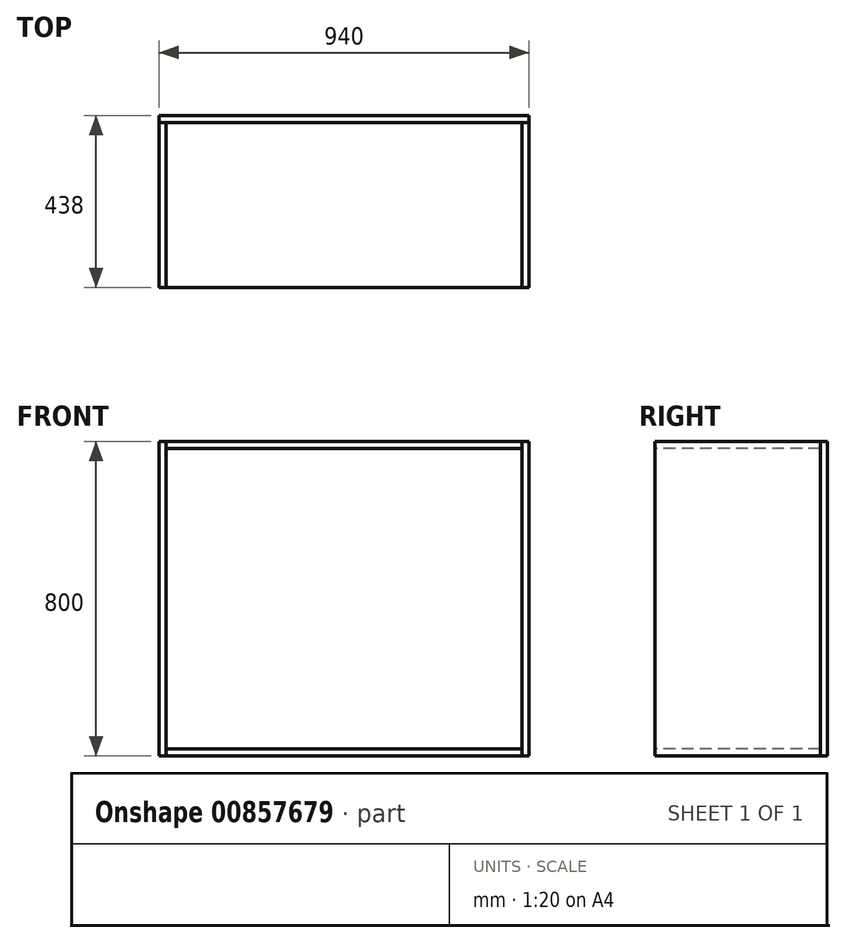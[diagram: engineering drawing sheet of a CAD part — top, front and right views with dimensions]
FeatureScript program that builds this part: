
annotation { "Feature Type Name" : "Feature", "Feature Type Description" : "" }
export const myFeature = defineFeature(function(context is Context, id is Id, definition is map)
    precondition{}
    {
        {
            var Q0;
            Q0=qCreatedBy(makeId("Top.planeOp"),FACE);
            var sketch = newSketch(context, id + "F0", { "sketchPlane" : qUnion([Q0])});
            skLineSegment(sketch, "E0.bottom", {"start": v(470, -210) * mm, "end": v(-470, -210) * mm});
            skLineSegment(sketch, "E0.top", {"start": v(470, 210) * mm, "end": v(-470, 210) * mm});
            skLineSegment(sketch, "E0.left", {"start": v(470, -210) * mm, "end": v(470, 210) * mm});
            skLineSegment(sketch, "E0.right", {"start": v(-470, -210) * mm, "end": v(-470, 210) * mm});
            skPoint(sketch, "E0.middle", {"position": v(0, 0) * mm});
            skLineSegment(sketch, "E1.0", {"start": v(452, 192) * mm, "end": v(-452, 192) * mm});
            skLineSegment(sketch, "E1.1", {"start": v(452, -192) * mm, "end": v(452, 192) * mm});
            skLineSegment(sketch, "E1.2", {"start": v(452, -192) * mm, "end": v(-452, -192) * mm});
            skLineSegment(sketch, "E1.3", {"start": v(-452, -192) * mm, "end": v(-452, 192) * mm});
            skLineSegment(sketch, "E2", {"start": v(-452, -192) * mm, "end": v(-452, -210) * mm});
            skLineSegment(sketch, "E3", {"start": v(-452, 192) * mm, "end": v(-452, 210) * mm});
            skLineSegment(sketch, "E4", {"start": v(452, 192) * mm, "end": v(452, 210) * mm});
            skLineSegment(sketch, "E5", {"start": v(452, -192) * mm, "end": v(452, -210) * mm});
            skSolve(sketch);
        }
        {
            var Q0;
            {var subQ0=sQuery(id+"F0.wireOp",EDGE,"E0.right");Q0=makeQuery(id+"F0.imprint","IMPRINT",FACE,{"disambiguationData":[TD([[makeQuery(id+"F0.imprint","IMPRINT",EDGE,{"derivedFrom":subQ0}),-1.0]])]});}
            var Q1;
            {var subQ0=sQuery(id+"F0.wireOp",EDGE,"E0.left");Q1=makeQuery(id+"F0.imprint","IMPRINT",FACE,{"disambiguationData":[TD([[makeQuery(id+"F0.imprint","IMPRINT",EDGE,{"derivedFrom":subQ0}),1.0]])]});}
            extrude(context, id + "F1", {"entities" : qUnion([Q0, Q1]), "depth" : 800 * mm, "offsetDistance" : 25 * mm});
        }
        {
            var Q0;
            Q0=makeQuery(id+"F1.opExtrude","CAP_FACE",FACE,{"disambiguationData":[OSD([sQuery(id+"F0.wireOp",EDGE,"E0.bottom"),sQuery(id+"F0.wireOp",EDGE,"E0.top"),sQuery(id+"F0.wireOp",EDGE,"E0.right"),sQuery(id+"F0.wireOp",EDGE,"E1.3"),sQuery(id+"F0.wireOp",EDGE,"E2"),sQuery(id+"F0.wireOp",EDGE,"E3")])],"isStart":false});
            var sketch = newSketch(context, id + "F2", { "sketchPlane" : qUnion([Q0])});
            skLineSegment(sketch, "E6.bottom", {"start": v(-452, -210) * mm, "end": v(452, -210) * mm});
            skLineSegment(sketch, "E6.top", {"start": v(-452, 210) * mm, "end": v(452, 210) * mm});
            skLineSegment(sketch, "E6.left", {"start": v(-452, -210) * mm, "end": v(-452, 210) * mm});
            skLineSegment(sketch, "E6.right", {"start": v(452, -210) * mm, "end": v(452, 210) * mm});
            skSolve(sketch);
        }
        {
            var Q0;
            Q0=makeQuery(id+"F2.imprint","IMPRINT",FACE,{"disambiguationData":[TD([[makeQuery(id+"F2.imprint","IMPRINT",EDGE,{"derivedFrom":sQuery(id+"F2.wireOp",EDGE,"E6.bottom")}),1.0]])]});
            extrude(context, id + "F3", {"entities" : qUnion([Q0]), "oppositeDirection" : true, "depth" : 18 * mm, "offsetDistance" : 25 * mm});
        }
        {
            var Q0;
            {var subQ0=sQuery(id+"F0.wireOp",EDGE,"E0.right");Q0=makeQuery(id+"F0.imprint","IMPRINT",FACE,{"disambiguationData":[TD([[makeQuery(id+"F0.imprint","IMPRINT",EDGE,{"derivedFrom":subQ0}),-1.0]])]});}
            var sketch = newSketch(context, id + "F4", { "sketchPlane" : qUnion([Q0])});
            skLineSegment(sketch, "E7.bottom", {"start": v(-452, -210) * mm, "end": v(452, -210) * mm});
            skLineSegment(sketch, "E7.top", {"start": v(-452, 210) * mm, "end": v(452, 210) * mm});
            skLineSegment(sketch, "E7.left", {"start": v(-452, -210) * mm, "end": v(-452, 210) * mm});
            skLineSegment(sketch, "E7.right", {"start": v(452, -210) * mm, "end": v(452, 210) * mm});
            skSolve(sketch);
        }
        {
            var Q0;
            {var subQ6=sQuery(id+"F4.wireOp",EDGE,"E7.bottom");Q0=makeQuery(id+"F4.imprint","IMPRINT",FACE,{"disambiguationData":[TD([[makeQuery(id+"F4.imprint","IMPRINT",EDGE,{"derivedFrom":subQ6}),1.0]])]});}
            extrude(context, id + "F5", {"entities" : qUnion([Q0]), "depth" : 18 * mm, "offsetDistance" : 25 * mm});
        }
        {
            var Q0;
            Q0=makeQuery(id+"F3.opExtrude","SWEPT_FACE",FACE,{"disambiguationData":[OSD([sQuery(id+"F2.wireOp",EDGE,"E6.top")])]});
            var sketch = newSketch(context, id + "F6", { "sketchPlane" : qUnion([Q0])});
            skLineSegment(sketch, "E8.bottom", {"start": v(-470, 800) * mm, "end": v(470, 800) * mm});
            skLineSegment(sketch, "E8.top", {"start": v(-470, 0) * mm, "end": v(470, 0) * mm});
            skLineSegment(sketch, "E8.left", {"start": v(-470, 800) * mm, "end": v(-470, 0) * mm});
            skLineSegment(sketch, "E8.right", {"start": v(470, 800) * mm, "end": v(470, 0) * mm});
            skSolve(sketch);
        }
        {
            var Q0;
            Q0=makeQuery(id+"F6.imprint","IMPRINT",FACE,{"disambiguationData":[TD([[makeQuery(id+"F6.imprint","IMPRINT",EDGE,{"derivedFrom":sQuery(id+"F6.wireOp",EDGE,"E8.top")}),1.0]])]});
            var Q1;
            {var subQ1=sQuery(id+"F2.wireOp",EDGE,"E6.top");Q1=makeQuery(id+"F6.imprint","IMPRINT",FACE,{"disambiguationData":[TD([[makeQuery(id+"F6.imprint","IMPRINT",EDGE,{"derivedFrom":makeQuery(id+"F3.opExtrude","CAP_EDGE",EDGE,{"disambiguationData":[OSD([subQ1])],"isStart":false})}),-1.0]])]});}
            extrude(context, id + "F7", {"entities" : qUnion([Q0, Q1]), "depth" : 18 * mm, "offsetDistance" : 25 * mm});
        }
    });
